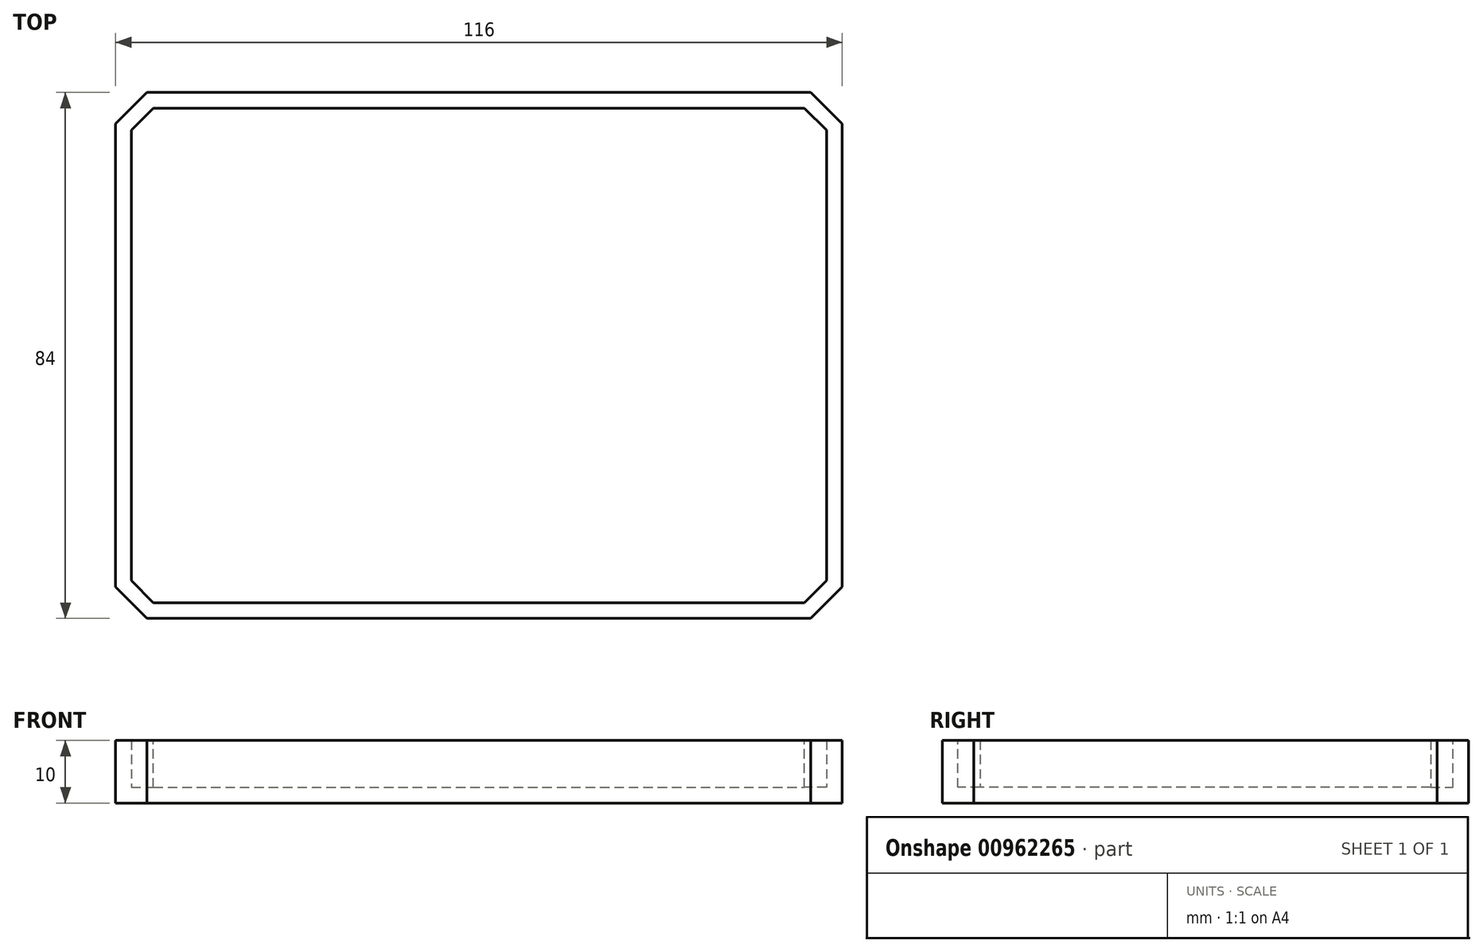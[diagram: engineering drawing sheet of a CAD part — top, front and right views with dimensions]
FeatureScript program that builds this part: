
annotation { "Feature Type Name" : "Feature", "Feature Type Description" : "" }
export const myFeature = defineFeature(function(context is Context, id is Id, definition is map)
    precondition{}
    {
        {
            var Q0;
            Q0=qCreatedBy(makeId("Top.planeOp"),FACE);
            var sketch = newSketch(context, id + "F0", { "sketchPlane" : qUnion([Q0])});
            skLineSegment(sketch, "E0.bottom", {"start": v(-60.75, 42.2) * mm, "end": v(55.25, 42.2) * mm});
            skLineSegment(sketch, "E0.top", {"start": v(-60.75, -41.8) * mm, "end": v(55.25, -41.8) * mm});
            skLineSegment(sketch, "E0.left", {"start": v(-60.75, 42.2) * mm, "end": v(-60.75, -41.8) * mm});
            skLineSegment(sketch, "E0.right", {"start": v(55.25, 42.2) * mm, "end": v(55.25, -41.8) * mm});
            skSolve(sketch);
        }
        {
            var Q0;
            Q0=makeQuery(id+"F0.imprint","IMPRINT",FACE,{"disambiguationData":[TD([[makeQuery(id+"F0.imprint","IMPRINT",EDGE,{"derivedFrom":sQuery(id+"F0.wireOp",EDGE,"E0.bottom")}),-1.0]])]});
            extrude(context, id + "F1", {"entities" : qUnion([Q0]), "oppositeDirection" : true, "depth" : 10 * mm, "offsetDistance" : 25 * mm});
        }
        {
            var Q0;
            Q0=makeQuery(id+"F1.opExtrude","SWEPT_EDGE",EDGE,{"disambiguationData":[OSD([sQuery(id+"F0.wireOp",EDGE,"E0.top"),sQuery(id+"F0.wireOp",EDGE,"E0.right")])]});
            var Q1;
            Q1=makeQuery(id+"F1.opExtrude","SWEPT_EDGE",EDGE,{"disambiguationData":[OSD([sQuery(id+"F0.wireOp",EDGE,"E0.top"),sQuery(id+"F0.wireOp",EDGE,"E0.left")])]});
            var Q2;
            Q2=makeQuery(id+"F1.opExtrude","SWEPT_EDGE",EDGE,{"disambiguationData":[OSD([sQuery(id+"F0.wireOp",EDGE,"E0.bottom"),sQuery(id+"F0.wireOp",EDGE,"E0.right")])]});
            var Q3;
            Q3=makeQuery(id+"F1.opExtrude","SWEPT_EDGE",EDGE,{"disambiguationData":[OSD([sQuery(id+"F0.wireOp",EDGE,"E0.bottom"),sQuery(id+"F0.wireOp",EDGE,"E0.left")])]});
            chamfer(context, id + "F2", {"entities" : qUnion([Q0, Q1, Q2, Q3]), "width" : 5 * mm, "tangentPropagation" : true});
        }
        {
            var Q0;
            Q0=makeQuery(id+"F1.opExtrude","CAP_FACE",FACE,{"disambiguationData":[OSD([sQuery(id+"F0.wireOp",EDGE,"E0.bottom"),sQuery(id+"F0.wireOp",EDGE,"E0.top"),sQuery(id+"F0.wireOp",EDGE,"E0.left"),sQuery(id+"F0.wireOp",EDGE,"E0.right")])],"isStart":true});
            shell(context, id + "F3", {"entities" : qUnion([Q0]), "thickness" : 2.5 * mm});
        }
    });
